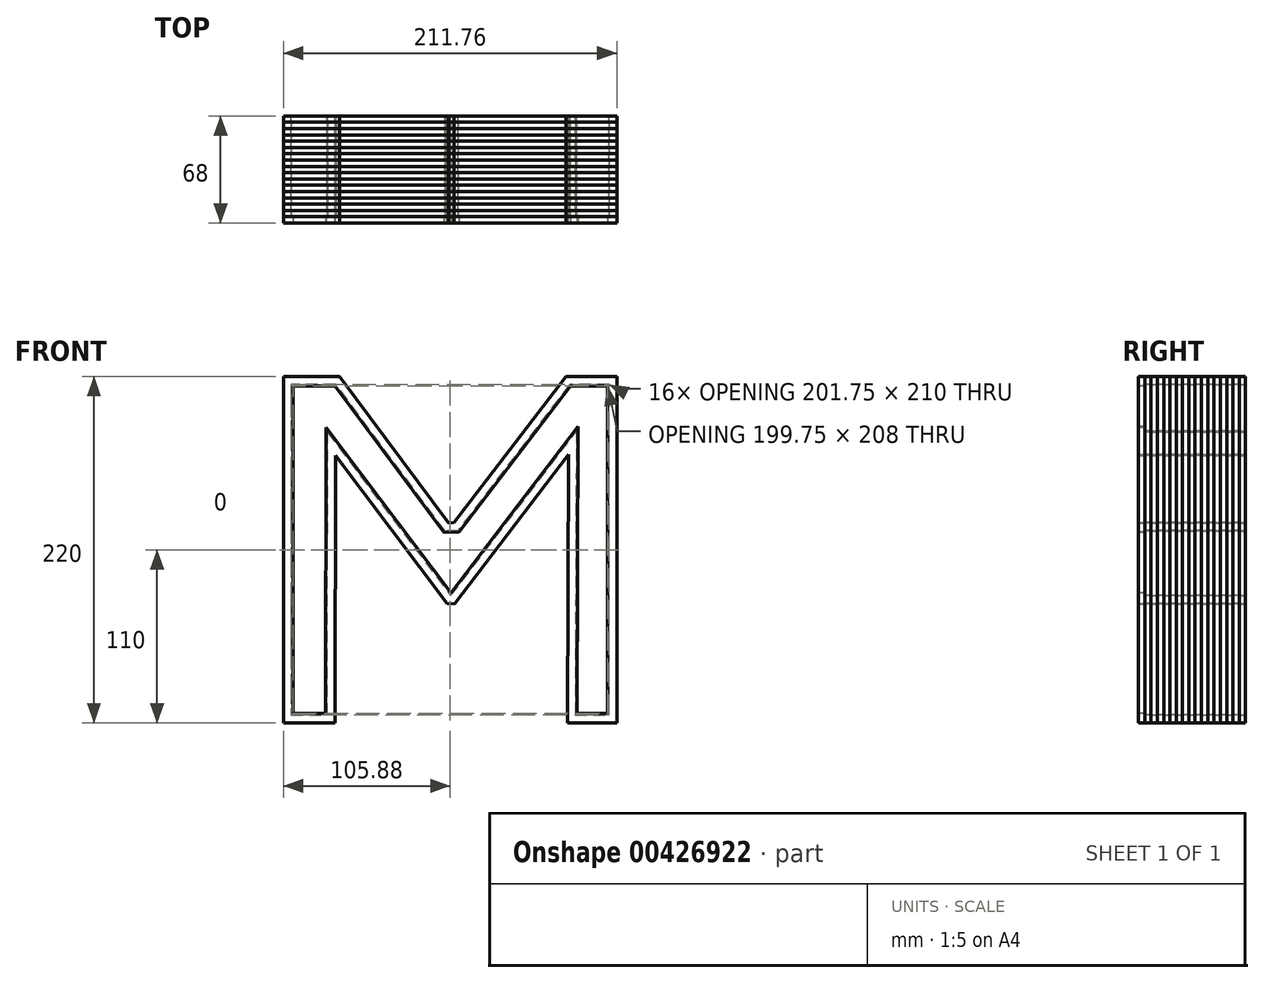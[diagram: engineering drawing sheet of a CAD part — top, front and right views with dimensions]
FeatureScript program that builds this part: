
annotation { "Feature Type Name" : "Feature", "Feature Type Description" : "" }
export const myFeature = defineFeature(function(context is Context, id is Id, definition is map)
    precondition{}
    {
        {
            var Q0;
            Q0=qCreatedBy(makeId("Front.planeOp"),FACE);
            var sketch = newSketch(context, id + "F0", { "sketchPlane" : qUnion([Q0])});
            skLineSegment(sketch, "E0", {"start": v(-105.88, -110) * mm, "end": v(-105.88, 110) * mm});
            skLineSegment(sketch, "E1", {"start": v(-105.88, 110) * mm, "end": v(-70.09, 110) * mm});
            skLineSegment(sketch, "E2", {"start": v(-70.09, 110) * mm, "end": v(-0.97, 17.02) * mm});
            skLineSegment(sketch, "E3", {"start": v(-0.97, 17.02) * mm, "end": v(2.54, 17.2) * mm});
            skLineSegment(sketch, "E4", {"start": v(2.54, 17.2) * mm, "end": v(73.6, 110) * mm});
            skLineSegment(sketch, "E5", {"start": v(73.6, 110) * mm, "end": v(105.88, 110) * mm});
            skLineSegment(sketch, "E6", {"start": v(105.88, 110) * mm, "end": v(105.88, -110) * mm});
            skLineSegment(sketch, "E7", {"start": v(105.88, -110) * mm, "end": v(74.47, -110) * mm});
            skLineSegment(sketch, "E8", {"start": v(74.47, -110) * mm, "end": v(75.18, 60.53) * mm});
            skLineSegment(sketch, "E9", {"start": v(75.18, 60.53) * mm, "end": v(2.78, -34.32) * mm});
            skLineSegment(sketch, "E10", {"start": v(2.78, -34.32) * mm, "end": v(-2.02, -34.2) * mm});
            skLineSegment(sketch, "E11", {"start": v(-2.02, -34.2) * mm, "end": v(-72.9, 59.82) * mm});
            skLineSegment(sketch, "E12", {"start": v(-72.9, 59.82) * mm, "end": v(-73.25, -110) * mm});
            skLineSegment(sketch, "E13", {"start": v(-73.25, -110) * mm, "end": v(-105.88, -110) * mm});
            skSolve(sketch);
        }
        {
            var Q0;
            Q0=makeQuery(id+"F0.imprint","IMPRINT",FACE,{"disambiguationData":[TD([[makeQuery(id+"F0.imprint","IMPRINT",EDGE,{"derivedFrom":sQuery(id+"F0.wireOp",EDGE,"E0")}),-1.0]])]});
            extrude(context, id + "F1", {"entities" : qUnion([Q0]), "depth" : 4 * mm});
        }
        {
            var Q0;
            Q0=makeQuery(id+"F1.opExtrude","CAP_FACE",FACE,{"disambiguationData":[OSD([sQuery(id+"F0.wireOp",EDGE,"E0"),sQuery(id+"F0.wireOp",EDGE,"E1"),sQuery(id+"F0.wireOp",EDGE,"E2"),sQuery(id+"F0.wireOp",EDGE,"E3"),sQuery(id+"F0.wireOp",EDGE,"E4"),sQuery(id+"F0.wireOp",EDGE,"E5"),sQuery(id+"F0.wireOp",EDGE,"E6"),sQuery(id+"F0.wireOp",EDGE,"E7"),sQuery(id+"F0.wireOp",EDGE,"E8"),sQuery(id+"F0.wireOp",EDGE,"E9"),sQuery(id+"F0.wireOp",EDGE,"E10"),sQuery(id+"F0.wireOp",EDGE,"E11"),sQuery(id+"F0.wireOp",EDGE,"E12"),sQuery(id+"F0.wireOp",EDGE,"E13")])],"isStart":false});
            var sketch = newSketch(context, id + "F2", { "sketchPlane" : qUnion([Q0])});
            skLineSegment(sketch, "E14.0", {"start": v(-99.88, 104) * mm, "end": v(-99.88, -104) * mm});
            skLineSegment(sketch, "E14.1", {"start": v(-73.1, 104) * mm, "end": v(-99.88, 104) * mm});
            skLineSegment(sketch, "E14.2", {"start": v(81.25, 78.37) * mm, "end": v(80.5, -104) * mm});
            skLineSegment(sketch, "E14.3", {"start": v(0.43, -27.5) * mm, "end": v(81.25, 78.37) * mm});
            skLineSegment(sketch, "E14.4", {"start": v(-78.86, 77.7) * mm, "end": v(0.43, -27.5) * mm});
            skLineSegment(sketch, "E14.5", {"start": v(-79.24, -104) * mm, "end": v(-78.86, 77.7) * mm});
            skLineSegment(sketch, "E14.6", {"start": v(80.5, -104) * mm, "end": v(99.88, -104) * mm});
            skLineSegment(sketch, "E14.7", {"start": v(99.88, -104) * mm, "end": v(99.88, 104) * mm});
            skLineSegment(sketch, "E14.8", {"start": v(-99.88, -104) * mm, "end": v(-79.24, -104) * mm});
            skLineSegment(sketch, "E14.9", {"start": v(99.88, 104) * mm, "end": v(76.55, 104) * mm});
            skLineSegment(sketch, "E14.10", {"start": v(76.55, 104) * mm, "end": v(5.61, 11.34) * mm});
            skLineSegment(sketch, "E14.11", {"start": v(5.61, 11.34) * mm, "end": v(-3.87, 10.87) * mm});
            skLineSegment(sketch, "E14.12", {"start": v(-3.87, 10.87) * mm, "end": v(-73.1, 104) * mm});
            skSolve(sketch);
        }
        {
            var Q0;
            Q0=makeQuery(id+"F2.imprint","IMPRINT",FACE,{"disambiguationData":[TD([[makeQuery(id+"F2.imprint","IMPRINT",EDGE,{"derivedFrom":sQuery(id+"F2.wireOp",EDGE,"E14.0")}),1.0]])]});
            extrude(context, id + "F3", {"entities" : qUnion([Q0]), "operationType" : NewBodyOperationType.REMOVE, "oppositeDirection" : true, "depth" : 25 * mm});
        }
        {
            var Q0;
            Q0=makeQuery(id+"F1.opExtrude","CAP_FACE",FACE,{"disambiguationData":[OSD([sQuery(id+"F0.wireOp",EDGE,"E0"),sQuery(id+"F0.wireOp",EDGE,"E1"),sQuery(id+"F0.wireOp",EDGE,"E2"),sQuery(id+"F0.wireOp",EDGE,"E3"),sQuery(id+"F0.wireOp",EDGE,"E4"),sQuery(id+"F0.wireOp",EDGE,"E5"),sQuery(id+"F0.wireOp",EDGE,"E6"),sQuery(id+"F0.wireOp",EDGE,"E7"),sQuery(id+"F0.wireOp",EDGE,"E8"),sQuery(id+"F0.wireOp",EDGE,"E9"),sQuery(id+"F0.wireOp",EDGE,"E10"),sQuery(id+"F0.wireOp",EDGE,"E11"),sQuery(id+"F0.wireOp",EDGE,"E12"),sQuery(id+"F0.wireOp",EDGE,"E13")])],"isStart":true});
            var sketch = newSketch(context, id + "F4", { "sketchPlane" : qUnion([Q0])});
            skLineSegment(sketch, "E15.0", {"start": v(-2.54, 17.2) * mm, "end": v(-73.6, 110) * mm});
            skLineSegment(sketch, "E15.1", {"start": v(70.09, 110) * mm, "end": v(0.97, 17.02) * mm});
            skLineSegment(sketch, "E15.2", {"start": v(-75.18, 60.53) * mm, "end": v(-2.78, -34.32) * mm});
            skLineSegment(sketch, "E15.3", {"start": v(-74.47, -110) * mm, "end": v(-75.18, 60.53) * mm});
            skLineSegment(sketch, "E15.4", {"start": v(-105.88, -110) * mm, "end": v(-74.47, -110) * mm});
            skLineSegment(sketch, "E15.5", {"start": v(-105.88, 110) * mm, "end": v(-105.88, -110) * mm});
            skLineSegment(sketch, "E15.6", {"start": v(-2.78, -34.32) * mm, "end": v(2.02, -34.2) * mm});
            skLineSegment(sketch, "E15.7", {"start": v(2.02, -34.2) * mm, "end": v(72.9, 59.82) * mm});
            skLineSegment(sketch, "E15.9", {"start": v(72.9, 59.82) * mm, "end": v(73.25, -110) * mm});
            skLineSegment(sketch, "E15.10", {"start": v(73.25, -110) * mm, "end": v(105.88, -110) * mm});
            skLineSegment(sketch, "E15.11", {"start": v(105.88, -110) * mm, "end": v(105.88, 110) * mm});
            skLineSegment(sketch, "E15.12", {"start": v(105.88, 110) * mm, "end": v(70.09, 110) * mm});
            skLineSegment(sketch, "E16", {"start": v(-2.54, 17.2) * mm, "end": v(0.97, 17.02) * mm});
            skLineSegment(sketch, "E17", {"start": v(-105.88, 110) * mm, "end": v(-73.6, 110) * mm});
            skLineSegment(sketch, "E18.0", {"start": v(-100.88, -105) * mm, "end": v(-100.88, 105) * mm});
            skLineSegment(sketch, "E18.1", {"start": v(-79.5, -105) * mm, "end": v(-100.88, -105) * mm});
            skLineSegment(sketch, "E18.2", {"start": v(72.6, 105) * mm, "end": v(100.88, 105) * mm});
            skLineSegment(sketch, "E18.3", {"start": v(3.39, 11.9) * mm, "end": v(72.6, 105) * mm});
            skLineSegment(sketch, "E18.4", {"start": v(-5.1, 12.32) * mm, "end": v(3.39, 11.9) * mm});
            skLineSegment(sketch, "E18.5", {"start": v(-76.06, 105) * mm, "end": v(-5.1, 12.32) * mm});
            skLineSegment(sketch, "E18.6", {"start": v(100.88, 105) * mm, "end": v(100.88, -105) * mm});
            skLineSegment(sketch, "E18.7", {"start": v(100.88, -105) * mm, "end": v(78.24, -105) * mm});
            skLineSegment(sketch, "E18.8", {"start": v(-100.88, 105) * mm, "end": v(-76.06, 105) * mm});
            skLineSegment(sketch, "E18.9", {"start": v(78.24, -105) * mm, "end": v(77.86, 74.73) * mm});
            skLineSegment(sketch, "E18.10", {"start": v(77.86, 74.73) * mm, "end": v(-0.43, -29.15) * mm});
            skLineSegment(sketch, "E18.11", {"start": v(-0.43, -29.15) * mm, "end": v(-80.24, 75.4) * mm});
            skLineSegment(sketch, "E18.12", {"start": v(-80.24, 75.4) * mm, "end": v(-79.5, -105) * mm});
            skSolve(sketch);
        }
        {
            var Q0;
            Q0 = qSketchRegion(id + "F4", true);
            extrude(context, id + "F5", {"entities" : qUnion([Q0]), "depth" : 4 * mm});
        }
        {
            var Q0;
            Q0=makeQuery(id+"F5.opExtrude","SWEPT_BODY",BODY,{"disambiguationData":[OSD([sQuery(id+"F4.wireOp",EDGE,"E15.0"),sQuery(id+"F4.wireOp",EDGE,"E15.1"),sQuery(id+"F4.wireOp",EDGE,"E15.2"),sQuery(id+"F4.wireOp",EDGE,"E15.3"),sQuery(id+"F4.wireOp",EDGE,"E15.4"),sQuery(id+"F4.wireOp",EDGE,"E15.5"),sQuery(id+"F4.wireOp",EDGE,"E15.6"),sQuery(id+"F4.wireOp",EDGE,"E15.7"),sQuery(id+"F4.wireOp",EDGE,"E15.9"),sQuery(id+"F4.wireOp",EDGE,"E15.10"),sQuery(id+"F4.wireOp",EDGE,"E15.11"),sQuery(id+"F4.wireOp",EDGE,"E15.12"),sQuery(id+"F4.wireOp",EDGE,"E16"),sQuery(id+"F4.wireOp",EDGE,"E17"),sQuery(id+"F4.wireOp",EDGE,"E18.0"),sQuery(id+"F4.wireOp",EDGE,"E18.1"),sQuery(id+"F4.wireOp",EDGE,"E18.2"),sQuery(id+"F4.wireOp",EDGE,"E18.3"),sQuery(id+"F4.wireOp",EDGE,"E18.4"),sQuery(id+"F4.wireOp",EDGE,"E18.5"),sQuery(id+"F4.wireOp",EDGE,"E18.6"),sQuery(id+"F4.wireOp",EDGE,"E18.7"),sQuery(id+"F4.wireOp",EDGE,"E18.8"),sQuery(id+"F4.wireOp",EDGE,"E18.9"),sQuery(id+"F4.wireOp",EDGE,"E18.10"),sQuery(id+"F4.wireOp",EDGE,"E18.11"),sQuery(id+"F4.wireOp",EDGE,"E18.12")])]});
            var Q1;
            Q1=makeQuery(id+"F5.opExtrude","CAP_FACE",FACE,{"disambiguationData":[OSD([sQuery(id+"F4.wireOp",EDGE,"E15.0"),sQuery(id+"F4.wireOp",EDGE,"E15.1"),sQuery(id+"F4.wireOp",EDGE,"E15.2"),sQuery(id+"F4.wireOp",EDGE,"E15.3"),sQuery(id+"F4.wireOp",EDGE,"E15.4"),sQuery(id+"F4.wireOp",EDGE,"E15.5"),sQuery(id+"F4.wireOp",EDGE,"E15.6"),sQuery(id+"F4.wireOp",EDGE,"E15.7"),sQuery(id+"F4.wireOp",EDGE,"E15.9"),sQuery(id+"F4.wireOp",EDGE,"E15.10"),sQuery(id+"F4.wireOp",EDGE,"E15.11"),sQuery(id+"F4.wireOp",EDGE,"E15.12"),sQuery(id+"F4.wireOp",EDGE,"E16"),sQuery(id+"F4.wireOp",EDGE,"E17"),sQuery(id+"F4.wireOp",EDGE,"E18.0"),sQuery(id+"F4.wireOp",EDGE,"E18.1"),sQuery(id+"F4.wireOp",EDGE,"E18.2"),sQuery(id+"F4.wireOp",EDGE,"E18.3"),sQuery(id+"F4.wireOp",EDGE,"E18.4"),sQuery(id+"F4.wireOp",EDGE,"E18.5"),sQuery(id+"F4.wireOp",EDGE,"E18.6"),sQuery(id+"F4.wireOp",EDGE,"E18.7"),sQuery(id+"F4.wireOp",EDGE,"E18.8"),sQuery(id+"F4.wireOp",EDGE,"E18.9"),sQuery(id+"F4.wireOp",EDGE,"E18.10"),sQuery(id+"F4.wireOp",EDGE,"E18.11"),sQuery(id+"F4.wireOp",EDGE,"E18.12")])],"isStart":false});
            mirror(context, id + "F6", {"entities" : qUnion([Q0]), "mirrorPlane" : qUnion([Q1])});
        }
        {
            var Q0;
            Q0=makeQuery(id+"F6.opPattern","COPY",BODY,{"derivedFrom":makeQuery(id+"F5.opExtrude","SWEPT_BODY",BODY,{"disambiguationData":[OSD([sQuery(id+"F4.wireOp",EDGE,"E15.0"),sQuery(id+"F4.wireOp",EDGE,"E15.1"),sQuery(id+"F4.wireOp",EDGE,"E15.2"),sQuery(id+"F4.wireOp",EDGE,"E15.3"),sQuery(id+"F4.wireOp",EDGE,"E15.4"),sQuery(id+"F4.wireOp",EDGE,"E15.5"),sQuery(id+"F4.wireOp",EDGE,"E15.6"),sQuery(id+"F4.wireOp",EDGE,"E15.7"),sQuery(id+"F4.wireOp",EDGE,"E15.9"),sQuery(id+"F4.wireOp",EDGE,"E15.10"),sQuery(id+"F4.wireOp",EDGE,"E15.11"),sQuery(id+"F4.wireOp",EDGE,"E15.12"),sQuery(id+"F4.wireOp",EDGE,"E16"),sQuery(id+"F4.wireOp",EDGE,"E17"),sQuery(id+"F4.wireOp",EDGE,"E18.0"),sQuery(id+"F4.wireOp",EDGE,"E18.1"),sQuery(id+"F4.wireOp",EDGE,"E18.2"),sQuery(id+"F4.wireOp",EDGE,"E18.3"),sQuery(id+"F4.wireOp",EDGE,"E18.4"),sQuery(id+"F4.wireOp",EDGE,"E18.5"),sQuery(id+"F4.wireOp",EDGE,"E18.6"),sQuery(id+"F4.wireOp",EDGE,"E18.7"),sQuery(id+"F4.wireOp",EDGE,"E18.8"),sQuery(id+"F4.wireOp",EDGE,"E18.9"),sQuery(id+"F4.wireOp",EDGE,"E18.10"),sQuery(id+"F4.wireOp",EDGE,"E18.11"),sQuery(id+"F4.wireOp",EDGE,"E18.12")])]}),"instanceName":"1"});
            var Q1;
            Q1=makeQuery(id+"F5.opExtrude","SWEPT_BODY",BODY,{"disambiguationData":[OSD([sQuery(id+"F4.wireOp",EDGE,"E15.0"),sQuery(id+"F4.wireOp",EDGE,"E15.1"),sQuery(id+"F4.wireOp",EDGE,"E15.2"),sQuery(id+"F4.wireOp",EDGE,"E15.3"),sQuery(id+"F4.wireOp",EDGE,"E15.4"),sQuery(id+"F4.wireOp",EDGE,"E15.5"),sQuery(id+"F4.wireOp",EDGE,"E15.6"),sQuery(id+"F4.wireOp",EDGE,"E15.7"),sQuery(id+"F4.wireOp",EDGE,"E15.9"),sQuery(id+"F4.wireOp",EDGE,"E15.10"),sQuery(id+"F4.wireOp",EDGE,"E15.11"),sQuery(id+"F4.wireOp",EDGE,"E15.12"),sQuery(id+"F4.wireOp",EDGE,"E16"),sQuery(id+"F4.wireOp",EDGE,"E17"),sQuery(id+"F4.wireOp",EDGE,"E18.0"),sQuery(id+"F4.wireOp",EDGE,"E18.1"),sQuery(id+"F4.wireOp",EDGE,"E18.2"),sQuery(id+"F4.wireOp",EDGE,"E18.3"),sQuery(id+"F4.wireOp",EDGE,"E18.4"),sQuery(id+"F4.wireOp",EDGE,"E18.5"),sQuery(id+"F4.wireOp",EDGE,"E18.6"),sQuery(id+"F4.wireOp",EDGE,"E18.7"),sQuery(id+"F4.wireOp",EDGE,"E18.8"),sQuery(id+"F4.wireOp",EDGE,"E18.9"),sQuery(id+"F4.wireOp",EDGE,"E18.10"),sQuery(id+"F4.wireOp",EDGE,"E18.11"),sQuery(id+"F4.wireOp",EDGE,"E18.12")])]});
            var Q2;
            Q2=makeQuery(id+"F6.opPattern","COPY",FACE,{"derivedFrom":makeQuery(id+"F5.opExtrude","CAP_FACE",FACE,{"disambiguationData":[OSD([sQuery(id+"F4.wireOp",EDGE,"E15.0"),sQuery(id+"F4.wireOp",EDGE,"E15.1"),sQuery(id+"F4.wireOp",EDGE,"E15.2"),sQuery(id+"F4.wireOp",EDGE,"E15.3"),sQuery(id+"F4.wireOp",EDGE,"E15.4"),sQuery(id+"F4.wireOp",EDGE,"E15.5"),sQuery(id+"F4.wireOp",EDGE,"E15.6"),sQuery(id+"F4.wireOp",EDGE,"E15.7"),sQuery(id+"F4.wireOp",EDGE,"E15.9"),sQuery(id+"F4.wireOp",EDGE,"E15.10"),sQuery(id+"F4.wireOp",EDGE,"E15.11"),sQuery(id+"F4.wireOp",EDGE,"E15.12"),sQuery(id+"F4.wireOp",EDGE,"E16"),sQuery(id+"F4.wireOp",EDGE,"E17"),sQuery(id+"F4.wireOp",EDGE,"E18.0"),sQuery(id+"F4.wireOp",EDGE,"E18.1"),sQuery(id+"F4.wireOp",EDGE,"E18.2"),sQuery(id+"F4.wireOp",EDGE,"E18.3"),sQuery(id+"F4.wireOp",EDGE,"E18.4"),sQuery(id+"F4.wireOp",EDGE,"E18.5"),sQuery(id+"F4.wireOp",EDGE,"E18.6"),sQuery(id+"F4.wireOp",EDGE,"E18.7"),sQuery(id+"F4.wireOp",EDGE,"E18.8"),sQuery(id+"F4.wireOp",EDGE,"E18.9"),sQuery(id+"F4.wireOp",EDGE,"E18.10"),sQuery(id+"F4.wireOp",EDGE,"E18.11"),sQuery(id+"F4.wireOp",EDGE,"E18.12")])],"isStart":true}),"instanceName":"1"});
            mirror(context, id + "F7", {"entities" : qUnion([Q0, Q1]), "mirrorPlane" : qUnion([Q2])});
        }
        {
            var Q0;
            Q0=makeQuery(id+"F5.opExtrude","SWEPT_BODY",BODY,{"disambiguationData":[OSD([sQuery(id+"F4.wireOp",EDGE,"E15.0"),sQuery(id+"F4.wireOp",EDGE,"E15.1"),sQuery(id+"F4.wireOp",EDGE,"E15.2"),sQuery(id+"F4.wireOp",EDGE,"E15.3"),sQuery(id+"F4.wireOp",EDGE,"E15.4"),sQuery(id+"F4.wireOp",EDGE,"E15.5"),sQuery(id+"F4.wireOp",EDGE,"E15.6"),sQuery(id+"F4.wireOp",EDGE,"E15.7"),sQuery(id+"F4.wireOp",EDGE,"E15.9"),sQuery(id+"F4.wireOp",EDGE,"E15.10"),sQuery(id+"F4.wireOp",EDGE,"E15.11"),sQuery(id+"F4.wireOp",EDGE,"E15.12"),sQuery(id+"F4.wireOp",EDGE,"E16"),sQuery(id+"F4.wireOp",EDGE,"E17"),sQuery(id+"F4.wireOp",EDGE,"E18.0"),sQuery(id+"F4.wireOp",EDGE,"E18.1"),sQuery(id+"F4.wireOp",EDGE,"E18.2"),sQuery(id+"F4.wireOp",EDGE,"E18.3"),sQuery(id+"F4.wireOp",EDGE,"E18.4"),sQuery(id+"F4.wireOp",EDGE,"E18.5"),sQuery(id+"F4.wireOp",EDGE,"E18.6"),sQuery(id+"F4.wireOp",EDGE,"E18.7"),sQuery(id+"F4.wireOp",EDGE,"E18.8"),sQuery(id+"F4.wireOp",EDGE,"E18.9"),sQuery(id+"F4.wireOp",EDGE,"E18.10"),sQuery(id+"F4.wireOp",EDGE,"E18.11"),sQuery(id+"F4.wireOp",EDGE,"E18.12")])]});
            var Q1;
            Q1=makeQuery(id+"F6.opPattern","COPY",BODY,{"derivedFrom":makeQuery(id+"F5.opExtrude","SWEPT_BODY",BODY,{"disambiguationData":[OSD([sQuery(id+"F4.wireOp",EDGE,"E15.0"),sQuery(id+"F4.wireOp",EDGE,"E15.1"),sQuery(id+"F4.wireOp",EDGE,"E15.2"),sQuery(id+"F4.wireOp",EDGE,"E15.3"),sQuery(id+"F4.wireOp",EDGE,"E15.4"),sQuery(id+"F4.wireOp",EDGE,"E15.5"),sQuery(id+"F4.wireOp",EDGE,"E15.6"),sQuery(id+"F4.wireOp",EDGE,"E15.7"),sQuery(id+"F4.wireOp",EDGE,"E15.9"),sQuery(id+"F4.wireOp",EDGE,"E15.10"),sQuery(id+"F4.wireOp",EDGE,"E15.11"),sQuery(id+"F4.wireOp",EDGE,"E15.12"),sQuery(id+"F4.wireOp",EDGE,"E16"),sQuery(id+"F4.wireOp",EDGE,"E17"),sQuery(id+"F4.wireOp",EDGE,"E18.0"),sQuery(id+"F4.wireOp",EDGE,"E18.1"),sQuery(id+"F4.wireOp",EDGE,"E18.2"),sQuery(id+"F4.wireOp",EDGE,"E18.3"),sQuery(id+"F4.wireOp",EDGE,"E18.4"),sQuery(id+"F4.wireOp",EDGE,"E18.5"),sQuery(id+"F4.wireOp",EDGE,"E18.6"),sQuery(id+"F4.wireOp",EDGE,"E18.7"),sQuery(id+"F4.wireOp",EDGE,"E18.8"),sQuery(id+"F4.wireOp",EDGE,"E18.9"),sQuery(id+"F4.wireOp",EDGE,"E18.10"),sQuery(id+"F4.wireOp",EDGE,"E18.11"),sQuery(id+"F4.wireOp",EDGE,"E18.12")])]}),"instanceName":"1"});
            var Q2;
            Q2=makeQuery(id+"F7.opPattern","COPY",BODY,{"derivedFrom":makeQuery(id+"F6.opPattern","COPY",BODY,{"derivedFrom":makeQuery(id+"F5.opExtrude","SWEPT_BODY",BODY,{"disambiguationData":[OSD([sQuery(id+"F4.wireOp",EDGE,"E15.0"),sQuery(id+"F4.wireOp",EDGE,"E15.1"),sQuery(id+"F4.wireOp",EDGE,"E15.2"),sQuery(id+"F4.wireOp",EDGE,"E15.3"),sQuery(id+"F4.wireOp",EDGE,"E15.4"),sQuery(id+"F4.wireOp",EDGE,"E15.5"),sQuery(id+"F4.wireOp",EDGE,"E15.6"),sQuery(id+"F4.wireOp",EDGE,"E15.7"),sQuery(id+"F4.wireOp",EDGE,"E15.9"),sQuery(id+"F4.wireOp",EDGE,"E15.10"),sQuery(id+"F4.wireOp",EDGE,"E15.11"),sQuery(id+"F4.wireOp",EDGE,"E15.12"),sQuery(id+"F4.wireOp",EDGE,"E16"),sQuery(id+"F4.wireOp",EDGE,"E17"),sQuery(id+"F4.wireOp",EDGE,"E18.0"),sQuery(id+"F4.wireOp",EDGE,"E18.1"),sQuery(id+"F4.wireOp",EDGE,"E18.2"),sQuery(id+"F4.wireOp",EDGE,"E18.3"),sQuery(id+"F4.wireOp",EDGE,"E18.4"),sQuery(id+"F4.wireOp",EDGE,"E18.5"),sQuery(id+"F4.wireOp",EDGE,"E18.6"),sQuery(id+"F4.wireOp",EDGE,"E18.7"),sQuery(id+"F4.wireOp",EDGE,"E18.8"),sQuery(id+"F4.wireOp",EDGE,"E18.9"),sQuery(id+"F4.wireOp",EDGE,"E18.10"),sQuery(id+"F4.wireOp",EDGE,"E18.11"),sQuery(id+"F4.wireOp",EDGE,"E18.12")])]}),"instanceName":"1"}),"instanceName":"1"});
            var Q3;
            Q3=makeQuery(id+"F7.opPattern","COPY",BODY,{"derivedFrom":makeQuery(id+"F5.opExtrude","SWEPT_BODY",BODY,{"disambiguationData":[OSD([sQuery(id+"F4.wireOp",EDGE,"E15.0"),sQuery(id+"F4.wireOp",EDGE,"E15.1"),sQuery(id+"F4.wireOp",EDGE,"E15.2"),sQuery(id+"F4.wireOp",EDGE,"E15.3"),sQuery(id+"F4.wireOp",EDGE,"E15.4"),sQuery(id+"F4.wireOp",EDGE,"E15.5"),sQuery(id+"F4.wireOp",EDGE,"E15.6"),sQuery(id+"F4.wireOp",EDGE,"E15.7"),sQuery(id+"F4.wireOp",EDGE,"E15.9"),sQuery(id+"F4.wireOp",EDGE,"E15.10"),sQuery(id+"F4.wireOp",EDGE,"E15.11"),sQuery(id+"F4.wireOp",EDGE,"E15.12"),sQuery(id+"F4.wireOp",EDGE,"E16"),sQuery(id+"F4.wireOp",EDGE,"E17"),sQuery(id+"F4.wireOp",EDGE,"E18.0"),sQuery(id+"F4.wireOp",EDGE,"E18.1"),sQuery(id+"F4.wireOp",EDGE,"E18.2"),sQuery(id+"F4.wireOp",EDGE,"E18.3"),sQuery(id+"F4.wireOp",EDGE,"E18.4"),sQuery(id+"F4.wireOp",EDGE,"E18.5"),sQuery(id+"F4.wireOp",EDGE,"E18.6"),sQuery(id+"F4.wireOp",EDGE,"E18.7"),sQuery(id+"F4.wireOp",EDGE,"E18.8"),sQuery(id+"F4.wireOp",EDGE,"E18.9"),sQuery(id+"F4.wireOp",EDGE,"E18.10"),sQuery(id+"F4.wireOp",EDGE,"E18.11"),sQuery(id+"F4.wireOp",EDGE,"E18.12")])]}),"instanceName":"1"});
            var Q4;
            Q4=makeQuery(id+"F7.opPattern","COPY",FACE,{"derivedFrom":makeQuery(id+"F5.opExtrude","CAP_FACE",FACE,{"disambiguationData":[OSD([sQuery(id+"F4.wireOp",EDGE,"E15.0"),sQuery(id+"F4.wireOp",EDGE,"E15.1"),sQuery(id+"F4.wireOp",EDGE,"E15.2"),sQuery(id+"F4.wireOp",EDGE,"E15.3"),sQuery(id+"F4.wireOp",EDGE,"E15.4"),sQuery(id+"F4.wireOp",EDGE,"E15.5"),sQuery(id+"F4.wireOp",EDGE,"E15.6"),sQuery(id+"F4.wireOp",EDGE,"E15.7"),sQuery(id+"F4.wireOp",EDGE,"E15.9"),sQuery(id+"F4.wireOp",EDGE,"E15.10"),sQuery(id+"F4.wireOp",EDGE,"E15.11"),sQuery(id+"F4.wireOp",EDGE,"E15.12"),sQuery(id+"F4.wireOp",EDGE,"E16"),sQuery(id+"F4.wireOp",EDGE,"E17"),sQuery(id+"F4.wireOp",EDGE,"E18.0"),sQuery(id+"F4.wireOp",EDGE,"E18.1"),sQuery(id+"F4.wireOp",EDGE,"E18.2"),sQuery(id+"F4.wireOp",EDGE,"E18.3"),sQuery(id+"F4.wireOp",EDGE,"E18.4"),sQuery(id+"F4.wireOp",EDGE,"E18.5"),sQuery(id+"F4.wireOp",EDGE,"E18.6"),sQuery(id+"F4.wireOp",EDGE,"E18.7"),sQuery(id+"F4.wireOp",EDGE,"E18.8"),sQuery(id+"F4.wireOp",EDGE,"E18.9"),sQuery(id+"F4.wireOp",EDGE,"E18.10"),sQuery(id+"F4.wireOp",EDGE,"E18.11"),sQuery(id+"F4.wireOp",EDGE,"E18.12")])],"isStart":true}),"instanceName":"1"});
            mirror(context, id + "F8", {"entities" : qUnion([Q0, Q1, Q2, Q3]), "mirrorPlane" : qUnion([Q4])});
        }
        {
            var Q0;
            Q0=makeQuery(id+"F8.opPattern","COPY",BODY,{"derivedFrom":makeQuery(id+"F5.opExtrude","SWEPT_BODY",BODY,{"disambiguationData":[OSD([sQuery(id+"F4.wireOp",EDGE,"E15.0"),sQuery(id+"F4.wireOp",EDGE,"E15.1"),sQuery(id+"F4.wireOp",EDGE,"E15.2"),sQuery(id+"F4.wireOp",EDGE,"E15.3"),sQuery(id+"F4.wireOp",EDGE,"E15.4"),sQuery(id+"F4.wireOp",EDGE,"E15.5"),sQuery(id+"F4.wireOp",EDGE,"E15.6"),sQuery(id+"F4.wireOp",EDGE,"E15.7"),sQuery(id+"F4.wireOp",EDGE,"E15.9"),sQuery(id+"F4.wireOp",EDGE,"E15.10"),sQuery(id+"F4.wireOp",EDGE,"E15.11"),sQuery(id+"F4.wireOp",EDGE,"E15.12"),sQuery(id+"F4.wireOp",EDGE,"E16"),sQuery(id+"F4.wireOp",EDGE,"E17"),sQuery(id+"F4.wireOp",EDGE,"E18.0"),sQuery(id+"F4.wireOp",EDGE,"E18.1"),sQuery(id+"F4.wireOp",EDGE,"E18.2"),sQuery(id+"F4.wireOp",EDGE,"E18.3"),sQuery(id+"F4.wireOp",EDGE,"E18.4"),sQuery(id+"F4.wireOp",EDGE,"E18.5"),sQuery(id+"F4.wireOp",EDGE,"E18.6"),sQuery(id+"F4.wireOp",EDGE,"E18.7"),sQuery(id+"F4.wireOp",EDGE,"E18.8"),sQuery(id+"F4.wireOp",EDGE,"E18.9"),sQuery(id+"F4.wireOp",EDGE,"E18.10"),sQuery(id+"F4.wireOp",EDGE,"E18.11"),sQuery(id+"F4.wireOp",EDGE,"E18.12")])]}),"instanceName":"1"});
            var Q1;
            Q1=makeQuery(id+"F8.opPattern","COPY",BODY,{"derivedFrom":makeQuery(id+"F6.opPattern","COPY",BODY,{"derivedFrom":makeQuery(id+"F5.opExtrude","SWEPT_BODY",BODY,{"disambiguationData":[OSD([sQuery(id+"F4.wireOp",EDGE,"E15.0"),sQuery(id+"F4.wireOp",EDGE,"E15.1"),sQuery(id+"F4.wireOp",EDGE,"E15.2"),sQuery(id+"F4.wireOp",EDGE,"E15.3"),sQuery(id+"F4.wireOp",EDGE,"E15.4"),sQuery(id+"F4.wireOp",EDGE,"E15.5"),sQuery(id+"F4.wireOp",EDGE,"E15.6"),sQuery(id+"F4.wireOp",EDGE,"E15.7"),sQuery(id+"F4.wireOp",EDGE,"E15.9"),sQuery(id+"F4.wireOp",EDGE,"E15.10"),sQuery(id+"F4.wireOp",EDGE,"E15.11"),sQuery(id+"F4.wireOp",EDGE,"E15.12"),sQuery(id+"F4.wireOp",EDGE,"E16"),sQuery(id+"F4.wireOp",EDGE,"E17"),sQuery(id+"F4.wireOp",EDGE,"E18.0"),sQuery(id+"F4.wireOp",EDGE,"E18.1"),sQuery(id+"F4.wireOp",EDGE,"E18.2"),sQuery(id+"F4.wireOp",EDGE,"E18.3"),sQuery(id+"F4.wireOp",EDGE,"E18.4"),sQuery(id+"F4.wireOp",EDGE,"E18.5"),sQuery(id+"F4.wireOp",EDGE,"E18.6"),sQuery(id+"F4.wireOp",EDGE,"E18.7"),sQuery(id+"F4.wireOp",EDGE,"E18.8"),sQuery(id+"F4.wireOp",EDGE,"E18.9"),sQuery(id+"F4.wireOp",EDGE,"E18.10"),sQuery(id+"F4.wireOp",EDGE,"E18.11"),sQuery(id+"F4.wireOp",EDGE,"E18.12")])]}),"instanceName":"1"}),"instanceName":"1"});
            var Q2;
            Q2=makeQuery(id+"F8.opPattern","COPY",BODY,{"derivedFrom":makeQuery(id+"F7.opPattern","COPY",BODY,{"derivedFrom":makeQuery(id+"F5.opExtrude","SWEPT_BODY",BODY,{"disambiguationData":[OSD([sQuery(id+"F4.wireOp",EDGE,"E15.0"),sQuery(id+"F4.wireOp",EDGE,"E15.1"),sQuery(id+"F4.wireOp",EDGE,"E15.2"),sQuery(id+"F4.wireOp",EDGE,"E15.3"),sQuery(id+"F4.wireOp",EDGE,"E15.4"),sQuery(id+"F4.wireOp",EDGE,"E15.5"),sQuery(id+"F4.wireOp",EDGE,"E15.6"),sQuery(id+"F4.wireOp",EDGE,"E15.7"),sQuery(id+"F4.wireOp",EDGE,"E15.9"),sQuery(id+"F4.wireOp",EDGE,"E15.10"),sQuery(id+"F4.wireOp",EDGE,"E15.11"),sQuery(id+"F4.wireOp",EDGE,"E15.12"),sQuery(id+"F4.wireOp",EDGE,"E16"),sQuery(id+"F4.wireOp",EDGE,"E17"),sQuery(id+"F4.wireOp",EDGE,"E18.0"),sQuery(id+"F4.wireOp",EDGE,"E18.1"),sQuery(id+"F4.wireOp",EDGE,"E18.2"),sQuery(id+"F4.wireOp",EDGE,"E18.3"),sQuery(id+"F4.wireOp",EDGE,"E18.4"),sQuery(id+"F4.wireOp",EDGE,"E18.5"),sQuery(id+"F4.wireOp",EDGE,"E18.6"),sQuery(id+"F4.wireOp",EDGE,"E18.7"),sQuery(id+"F4.wireOp",EDGE,"E18.8"),sQuery(id+"F4.wireOp",EDGE,"E18.9"),sQuery(id+"F4.wireOp",EDGE,"E18.10"),sQuery(id+"F4.wireOp",EDGE,"E18.11"),sQuery(id+"F4.wireOp",EDGE,"E18.12")])]}),"instanceName":"1"}),"instanceName":"1"});
            var Q3;
            Q3=makeQuery(id+"F7.opPattern","COPY",BODY,{"derivedFrom":makeQuery(id+"F5.opExtrude","SWEPT_BODY",BODY,{"disambiguationData":[OSD([sQuery(id+"F4.wireOp",EDGE,"E15.0"),sQuery(id+"F4.wireOp",EDGE,"E15.1"),sQuery(id+"F4.wireOp",EDGE,"E15.2"),sQuery(id+"F4.wireOp",EDGE,"E15.3"),sQuery(id+"F4.wireOp",EDGE,"E15.4"),sQuery(id+"F4.wireOp",EDGE,"E15.5"),sQuery(id+"F4.wireOp",EDGE,"E15.6"),sQuery(id+"F4.wireOp",EDGE,"E15.7"),sQuery(id+"F4.wireOp",EDGE,"E15.9"),sQuery(id+"F4.wireOp",EDGE,"E15.10"),sQuery(id+"F4.wireOp",EDGE,"E15.11"),sQuery(id+"F4.wireOp",EDGE,"E15.12"),sQuery(id+"F4.wireOp",EDGE,"E16"),sQuery(id+"F4.wireOp",EDGE,"E17"),sQuery(id+"F4.wireOp",EDGE,"E18.0"),sQuery(id+"F4.wireOp",EDGE,"E18.1"),sQuery(id+"F4.wireOp",EDGE,"E18.2"),sQuery(id+"F4.wireOp",EDGE,"E18.3"),sQuery(id+"F4.wireOp",EDGE,"E18.4"),sQuery(id+"F4.wireOp",EDGE,"E18.5"),sQuery(id+"F4.wireOp",EDGE,"E18.6"),sQuery(id+"F4.wireOp",EDGE,"E18.7"),sQuery(id+"F4.wireOp",EDGE,"E18.8"),sQuery(id+"F4.wireOp",EDGE,"E18.9"),sQuery(id+"F4.wireOp",EDGE,"E18.10"),sQuery(id+"F4.wireOp",EDGE,"E18.11"),sQuery(id+"F4.wireOp",EDGE,"E18.12")])]}),"instanceName":"1"});
            var Q4;
            Q4=makeQuery(id+"F5.opExtrude","SWEPT_BODY",BODY,{"disambiguationData":[OSD([sQuery(id+"F4.wireOp",EDGE,"E15.0"),sQuery(id+"F4.wireOp",EDGE,"E15.1"),sQuery(id+"F4.wireOp",EDGE,"E15.2"),sQuery(id+"F4.wireOp",EDGE,"E15.3"),sQuery(id+"F4.wireOp",EDGE,"E15.4"),sQuery(id+"F4.wireOp",EDGE,"E15.5"),sQuery(id+"F4.wireOp",EDGE,"E15.6"),sQuery(id+"F4.wireOp",EDGE,"E15.7"),sQuery(id+"F4.wireOp",EDGE,"E15.9"),sQuery(id+"F4.wireOp",EDGE,"E15.10"),sQuery(id+"F4.wireOp",EDGE,"E15.11"),sQuery(id+"F4.wireOp",EDGE,"E15.12"),sQuery(id+"F4.wireOp",EDGE,"E16"),sQuery(id+"F4.wireOp",EDGE,"E17"),sQuery(id+"F4.wireOp",EDGE,"E18.0"),sQuery(id+"F4.wireOp",EDGE,"E18.1"),sQuery(id+"F4.wireOp",EDGE,"E18.2"),sQuery(id+"F4.wireOp",EDGE,"E18.3"),sQuery(id+"F4.wireOp",EDGE,"E18.4"),sQuery(id+"F4.wireOp",EDGE,"E18.5"),sQuery(id+"F4.wireOp",EDGE,"E18.6"),sQuery(id+"F4.wireOp",EDGE,"E18.7"),sQuery(id+"F4.wireOp",EDGE,"E18.8"),sQuery(id+"F4.wireOp",EDGE,"E18.9"),sQuery(id+"F4.wireOp",EDGE,"E18.10"),sQuery(id+"F4.wireOp",EDGE,"E18.11"),sQuery(id+"F4.wireOp",EDGE,"E18.12")])]});
            var Q5;
            Q5=makeQuery(id+"F8.opPattern","COPY",BODY,{"derivedFrom":makeQuery(id+"F7.opPattern","COPY",BODY,{"derivedFrom":makeQuery(id+"F6.opPattern","COPY",BODY,{"derivedFrom":makeQuery(id+"F5.opExtrude","SWEPT_BODY",BODY,{"disambiguationData":[OSD([sQuery(id+"F4.wireOp",EDGE,"E15.0"),sQuery(id+"F4.wireOp",EDGE,"E15.1"),sQuery(id+"F4.wireOp",EDGE,"E15.2"),sQuery(id+"F4.wireOp",EDGE,"E15.3"),sQuery(id+"F4.wireOp",EDGE,"E15.4"),sQuery(id+"F4.wireOp",EDGE,"E15.5"),sQuery(id+"F4.wireOp",EDGE,"E15.6"),sQuery(id+"F4.wireOp",EDGE,"E15.7"),sQuery(id+"F4.wireOp",EDGE,"E15.9"),sQuery(id+"F4.wireOp",EDGE,"E15.10"),sQuery(id+"F4.wireOp",EDGE,"E15.11"),sQuery(id+"F4.wireOp",EDGE,"E15.12"),sQuery(id+"F4.wireOp",EDGE,"E16"),sQuery(id+"F4.wireOp",EDGE,"E17"),sQuery(id+"F4.wireOp",EDGE,"E18.0"),sQuery(id+"F4.wireOp",EDGE,"E18.1"),sQuery(id+"F4.wireOp",EDGE,"E18.2"),sQuery(id+"F4.wireOp",EDGE,"E18.3"),sQuery(id+"F4.wireOp",EDGE,"E18.4"),sQuery(id+"F4.wireOp",EDGE,"E18.5"),sQuery(id+"F4.wireOp",EDGE,"E18.6"),sQuery(id+"F4.wireOp",EDGE,"E18.7"),sQuery(id+"F4.wireOp",EDGE,"E18.8"),sQuery(id+"F4.wireOp",EDGE,"E18.9"),sQuery(id+"F4.wireOp",EDGE,"E18.10"),sQuery(id+"F4.wireOp",EDGE,"E18.11"),sQuery(id+"F4.wireOp",EDGE,"E18.12")])]}),"instanceName":"1"}),"instanceName":"1"}),"instanceName":"1"});
            var Q6;
            Q6=makeQuery(id+"F7.opPattern","COPY",BODY,{"derivedFrom":makeQuery(id+"F6.opPattern","COPY",BODY,{"derivedFrom":makeQuery(id+"F5.opExtrude","SWEPT_BODY",BODY,{"disambiguationData":[OSD([sQuery(id+"F4.wireOp",EDGE,"E15.0"),sQuery(id+"F4.wireOp",EDGE,"E15.1"),sQuery(id+"F4.wireOp",EDGE,"E15.2"),sQuery(id+"F4.wireOp",EDGE,"E15.3"),sQuery(id+"F4.wireOp",EDGE,"E15.4"),sQuery(id+"F4.wireOp",EDGE,"E15.5"),sQuery(id+"F4.wireOp",EDGE,"E15.6"),sQuery(id+"F4.wireOp",EDGE,"E15.7"),sQuery(id+"F4.wireOp",EDGE,"E15.9"),sQuery(id+"F4.wireOp",EDGE,"E15.10"),sQuery(id+"F4.wireOp",EDGE,"E15.11"),sQuery(id+"F4.wireOp",EDGE,"E15.12"),sQuery(id+"F4.wireOp",EDGE,"E16"),sQuery(id+"F4.wireOp",EDGE,"E17"),sQuery(id+"F4.wireOp",EDGE,"E18.0"),sQuery(id+"F4.wireOp",EDGE,"E18.1"),sQuery(id+"F4.wireOp",EDGE,"E18.2"),sQuery(id+"F4.wireOp",EDGE,"E18.3"),sQuery(id+"F4.wireOp",EDGE,"E18.4"),sQuery(id+"F4.wireOp",EDGE,"E18.5"),sQuery(id+"F4.wireOp",EDGE,"E18.6"),sQuery(id+"F4.wireOp",EDGE,"E18.7"),sQuery(id+"F4.wireOp",EDGE,"E18.8"),sQuery(id+"F4.wireOp",EDGE,"E18.9"),sQuery(id+"F4.wireOp",EDGE,"E18.10"),sQuery(id+"F4.wireOp",EDGE,"E18.11"),sQuery(id+"F4.wireOp",EDGE,"E18.12")])]}),"instanceName":"1"}),"instanceName":"1"});
            var Q7;
            Q7=makeQuery(id+"F6.opPattern","COPY",BODY,{"derivedFrom":makeQuery(id+"F5.opExtrude","SWEPT_BODY",BODY,{"disambiguationData":[OSD([sQuery(id+"F4.wireOp",EDGE,"E15.0"),sQuery(id+"F4.wireOp",EDGE,"E15.1"),sQuery(id+"F4.wireOp",EDGE,"E15.2"),sQuery(id+"F4.wireOp",EDGE,"E15.3"),sQuery(id+"F4.wireOp",EDGE,"E15.4"),sQuery(id+"F4.wireOp",EDGE,"E15.5"),sQuery(id+"F4.wireOp",EDGE,"E15.6"),sQuery(id+"F4.wireOp",EDGE,"E15.7"),sQuery(id+"F4.wireOp",EDGE,"E15.9"),sQuery(id+"F4.wireOp",EDGE,"E15.10"),sQuery(id+"F4.wireOp",EDGE,"E15.11"),sQuery(id+"F4.wireOp",EDGE,"E15.12"),sQuery(id+"F4.wireOp",EDGE,"E16"),sQuery(id+"F4.wireOp",EDGE,"E17"),sQuery(id+"F4.wireOp",EDGE,"E18.0"),sQuery(id+"F4.wireOp",EDGE,"E18.1"),sQuery(id+"F4.wireOp",EDGE,"E18.2"),sQuery(id+"F4.wireOp",EDGE,"E18.3"),sQuery(id+"F4.wireOp",EDGE,"E18.4"),sQuery(id+"F4.wireOp",EDGE,"E18.5"),sQuery(id+"F4.wireOp",EDGE,"E18.6"),sQuery(id+"F4.wireOp",EDGE,"E18.7"),sQuery(id+"F4.wireOp",EDGE,"E18.8"),sQuery(id+"F4.wireOp",EDGE,"E18.9"),sQuery(id+"F4.wireOp",EDGE,"E18.10"),sQuery(id+"F4.wireOp",EDGE,"E18.11"),sQuery(id+"F4.wireOp",EDGE,"E18.12")])]}),"instanceName":"1"});
            var Q8;
            Q8=makeQuery(id+"F8.opPattern","COPY",FACE,{"derivedFrom":makeQuery(id+"F5.opExtrude","CAP_FACE",FACE,{"disambiguationData":[OSD([sQuery(id+"F4.wireOp",EDGE,"E15.0"),sQuery(id+"F4.wireOp",EDGE,"E15.1"),sQuery(id+"F4.wireOp",EDGE,"E15.2"),sQuery(id+"F4.wireOp",EDGE,"E15.3"),sQuery(id+"F4.wireOp",EDGE,"E15.4"),sQuery(id+"F4.wireOp",EDGE,"E15.5"),sQuery(id+"F4.wireOp",EDGE,"E15.6"),sQuery(id+"F4.wireOp",EDGE,"E15.7"),sQuery(id+"F4.wireOp",EDGE,"E15.9"),sQuery(id+"F4.wireOp",EDGE,"E15.10"),sQuery(id+"F4.wireOp",EDGE,"E15.11"),sQuery(id+"F4.wireOp",EDGE,"E15.12"),sQuery(id+"F4.wireOp",EDGE,"E16"),sQuery(id+"F4.wireOp",EDGE,"E17"),sQuery(id+"F4.wireOp",EDGE,"E18.0"),sQuery(id+"F4.wireOp",EDGE,"E18.1"),sQuery(id+"F4.wireOp",EDGE,"E18.2"),sQuery(id+"F4.wireOp",EDGE,"E18.3"),sQuery(id+"F4.wireOp",EDGE,"E18.4"),sQuery(id+"F4.wireOp",EDGE,"E18.5"),sQuery(id+"F4.wireOp",EDGE,"E18.6"),sQuery(id+"F4.wireOp",EDGE,"E18.7"),sQuery(id+"F4.wireOp",EDGE,"E18.8"),sQuery(id+"F4.wireOp",EDGE,"E18.9"),sQuery(id+"F4.wireOp",EDGE,"E18.10"),sQuery(id+"F4.wireOp",EDGE,"E18.11"),sQuery(id+"F4.wireOp",EDGE,"E18.12")])],"isStart":true}),"instanceName":"1"});
            mirror(context, id + "F9", {"entities" : qUnion([Q0, Q1, Q2, Q3, Q4, Q5, Q6, Q7]), "mirrorPlane" : qUnion([Q8])});
        }
    });
